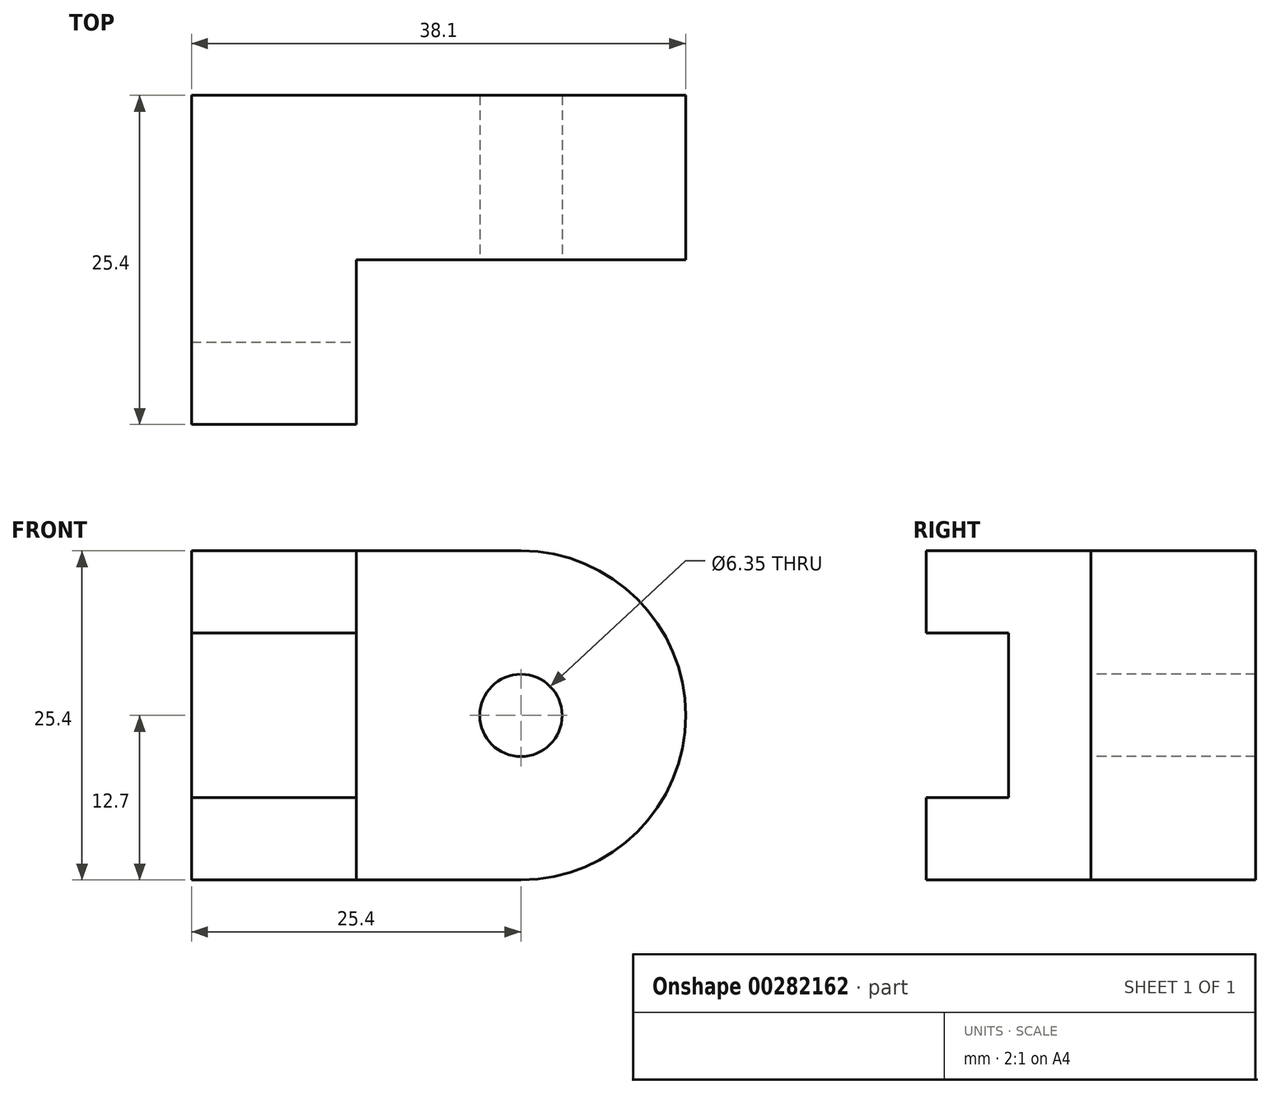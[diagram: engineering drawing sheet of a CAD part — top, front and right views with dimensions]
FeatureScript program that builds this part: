
annotation { "Feature Type Name" : "Feature", "Feature Type Description" : "" }
export const myFeature = defineFeature(function(context is Context, id is Id, definition is map)
    precondition{}
    {
        {
            var Q0;
            Q0=qCreatedBy(makeId("Front.planeOp"),FACE);
            var sketch = newSketch(context, id + "F0", { "sketchPlane" : qUnion([Q0])});
            skArc(sketch, "E0", {"start": v(0, -12.7) * mm, "mid": v(12.7, 0) * mm, "end": v(0, 12.7) * mm});
            skLineSegment(sketch, "E1", {"start": v(0, 12.7) * mm, "end": v(-12.7, 12.7) * mm});
            skLineSegment(sketch, "E2", {"start": v(-12.7, 12.7) * mm, "end": v(-12.7, -12.7) * mm});
            skLineSegment(sketch, "E3", {"start": v(-12.7, -12.7) * mm, "end": v(0, -12.7) * mm});
            skSolve(sketch);
        }
        {
            var Q0;
            Q0=makeQuery(id+"F0.imprint","IMPRINT",FACE,{"disambiguationData":[TD([[makeQuery(id+"F0.imprint","IMPRINT",EDGE,{"derivedFrom":sQuery(id+"F0.wireOp",EDGE,"E0")}),1.0]])]});
            extrude(context, id + "F1", {"entities" : qUnion([Q0]), "depth" : 12.7 * mm});
        }
        {
            var Q0;
            Q0=makeQuery(id+"F1.opExtrude","CAP_FACE",FACE,{"disambiguationData":[OSD([sQuery(id+"F0.wireOp",EDGE,"E0"),sQuery(id+"F0.wireOp",EDGE,"E1"),sQuery(id+"F0.wireOp",EDGE,"E2"),sQuery(id+"F0.wireOp",EDGE,"E3")])],"isStart":false});
            var sketch = newSketch(context, id + "F2", { "sketchPlane" : qUnion([Q0])});
            skCircle(sketch, "E4", {"center": v(0, 0) * mm, "radius": 3.18 * mm});
            skSolve(sketch);
        }
        {
            var Q0;
            Q0=makeQuery(id+"F2.imprint","IMPRINT",FACE,{"disambiguationData":[TD([[makeQuery(id+"F2.imprint","IMPRINT",EDGE,{"derivedFrom":sQuery(id+"F2.wireOp",EDGE,"E4")}),1.0]])]});
            extrude(context, id + "F3", {"entities" : qUnion([Q0]), "operationType" : NewBodyOperationType.REMOVE, "oppositeDirection" : true, "depth" : 25.4 * mm});
        }
        {
            var Q0;
            Q0=makeQuery(id+"F1.opExtrude","SWEPT_FACE",FACE,{"disambiguationData":[OSD([sQuery(id+"F0.wireOp",EDGE,"E2")])]});
            var sketch = newSketch(context, id + "F4", { "sketchPlane" : qUnion([Q0])});
            skLineSegment(sketch, "E5", {"start": v(0, 12.7) * mm, "end": v(25.4, 12.7) * mm});
            skPoint(sketch, "E5.endSnap0", {"position": v(6.35, 12.7) * mm});
            skLineSegment(sketch, "E6", {"start": v(25.4, 12.7) * mm, "end": v(25.4, -12.7) * mm});
            skLineSegment(sketch, "E7", {"start": v(25.4, -12.7) * mm, "end": v(0, -12.7) * mm});
            skLineSegment(sketch, "E8", {"start": v(0, -12.7) * mm, "end": v(0, 12.7) * mm});
            skSolve(sketch);
        }
        {
            var Q0;
            {var subQ0=sQuery(id+"F4.wireOp",EDGE,"E8");Q0=makeQuery(id+"F4.imprint","IMPRINT",FACE,{"disambiguationData":[TD([[makeQuery(id+"F4.imprint","IMPRINT",EDGE,{"derivedFrom":subQ0}),1.0]])]});}
            var Q1;
            {var subQ2=sQuery(id+"F4.wireOp",EDGE,"E6");Q1=makeQuery(id+"F4.imprint","IMPRINT",FACE,{"disambiguationData":[TD([[makeQuery(id+"F4.imprint","IMPRINT",EDGE,{"derivedFrom":subQ2}),-1.0]])]});}
            extrude(context, id + "F5", {"entities" : qUnion([Q0, Q1]), "operationType" : NewBodyOperationType.ADD, "depth" : 12.7 * mm});
        }
        {
            var Q0;
            Q0=makeQuery(id+"F5.opExtrude","SWEPT_FACE",FACE,{"disambiguationData":[OSD([sQuery(id+"F4.wireOp",EDGE,"E6")])]});
            var sketch = newSketch(context, id + "F6", { "sketchPlane" : qUnion([Q0])});
            skLineSegment(sketch, "E9.bottom", {"start": v(-25.4, 6.35) * mm, "end": v(-12.7, 6.35) * mm});
            skLineSegment(sketch, "E9.top", {"start": v(-25.4, -6.35) * mm, "end": v(-12.7, -6.35) * mm});
            skLineSegment(sketch, "E9.left", {"start": v(-25.4, 6.35) * mm, "end": v(-25.4, -6.35) * mm});
            skLineSegment(sketch, "E9.right", {"start": v(-12.7, 6.35) * mm, "end": v(-12.7, -6.35) * mm});
            skSolve(sketch);
        }
        {
            var Q0;
            Q0=makeQuery(id+"F6.imprint","IMPRINT",FACE,{"disambiguationData":[TD([[makeQuery(id+"F6.imprint","IMPRINT",EDGE,{"derivedFrom":sQuery(id+"F6.wireOp",EDGE,"E9.bottom")}),-1.0]])]});
            extrude(context, id + "F7", {"entities" : qUnion([Q0]), "operationType" : NewBodyOperationType.REMOVE, "oppositeDirection" : true, "depth" : 6.35 * mm});
        }
    });
